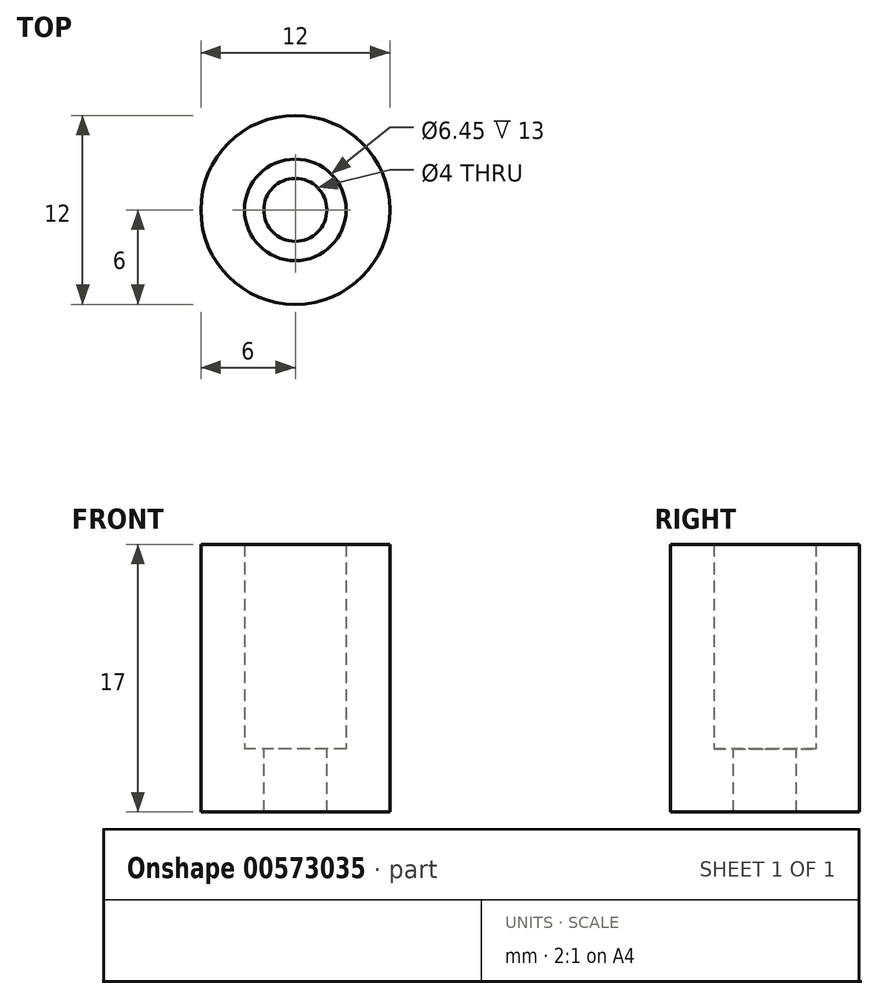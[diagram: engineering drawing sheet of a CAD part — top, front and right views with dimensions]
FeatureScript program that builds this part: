
annotation { "Feature Type Name" : "Feature", "Feature Type Description" : "" }
export const myFeature = defineFeature(function(context is Context, id is Id, definition is map)
    precondition{}
    {
        {
            var Q0;
            Q0=qCreatedBy(makeId("Top.planeOp"),FACE);
            var sketch = newSketch(context, id + "F0", { "sketchPlane" : qUnion([Q0])});
            skCircle(sketch, "E0", {"center": v(0, 0) * mm, "radius": 6 * mm});
            skCircle(sketch, "E1", {"center": v(0, 0) * mm, "radius": 3.23 * mm});
            skSolve(sketch);
        }
        {
            var Q0;
            Q0 = qSketchRegion(id + "F0", true);
            extrude(context, id + "F1", {"entities" : qUnion([Q0]), "depth" : 13 * mm, "offsetDistance" : 25 * mm});
        }
        {
            var Q0;
            Q0=qCreatedBy(makeId("Top.planeOp"),FACE);
            var sketch = newSketch(context, id + "F2", { "sketchPlane" : qUnion([Q0])});
            skCircle(sketch, "E2", {"center": v(0, 0) * mm, "radius": 6 * mm});
            skCircle(sketch, "E3", {"center": v(0, 0) * mm, "radius": 2 * mm});
            skSolve(sketch);
        }
        {
            var Q0;
            Q0 = qSketchRegion(id + "F2", true);
            extrude(context, id + "F3", {"entities" : qUnion([Q0]), "operationType" : NewBodyOperationType.ADD, "depth" : -4 * mm, "offsetDistance" : 25 * mm});
        }
    });
